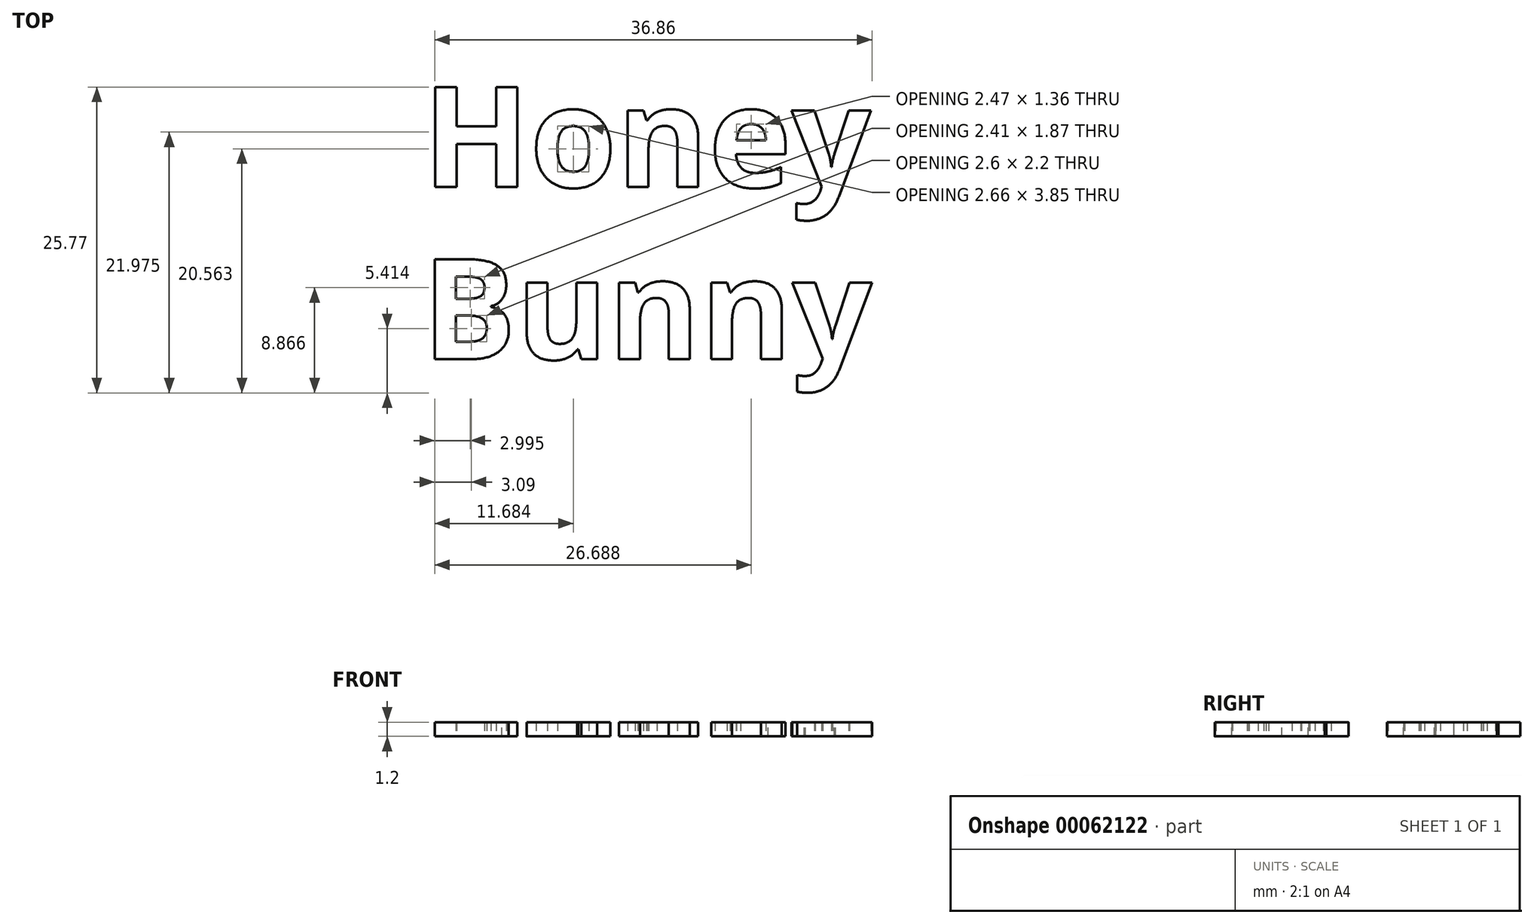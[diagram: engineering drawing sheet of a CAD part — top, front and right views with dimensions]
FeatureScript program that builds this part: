
annotation { "Feature Type Name" : "Feature", "Feature Type Description" : "" }
export const myFeature = defineFeature(function(context is Context, id is Id, definition is map)
    precondition{}
    {
        {
            var Q0;
            Q0=qCreatedBy(makeId("Top.planeOp"),FACE);
            var sketch = newSketch(context, id + "F0", { "sketchPlane" : qUnion([Q0])});
            skText(sketch, "E0", { "text": "Honey", "fontName": "OpenSans-Bold.ttf"});
            const initialGuessF0  = {"E0": [-0.0189, 0.003, 1, 0, 0.0085]};
            skSetInitialGuess(sketch, initialGuessF0);
            skSolve(sketch);
        }
        {
            var Q0;
            Q0=qCreatedBy(makeId("Top.planeOp"),FACE);
            var sketch = newSketch(context, id + "F1", { "sketchPlane" : qUnion([Q0])});
            skText(sketch, "E1", { "text": "Bunny", "fontName": "OpenSans-Bold.ttf"});
            const initialGuessF1  = {"E1": [-0.01896, -0.0115, 1, 0, 0.0085]};
            skSetInitialGuess(sketch, initialGuessF1);
            skSolve(sketch);
        }
        {
            var Q0;
            Q0 = qSketchRegion(id + "F0", true);
            extrude(context, id + "F2", {"entities" : qUnion([Q0]), "depth" : 1.2 * mm});
        }
        {
            var Q0;
            Q0 = qSketchRegion(id + "F1", true);
            extrude(context, id + "F3", {"entities" : qUnion([Q0]), "depth" : 1.2 * mm});
        }
    });
